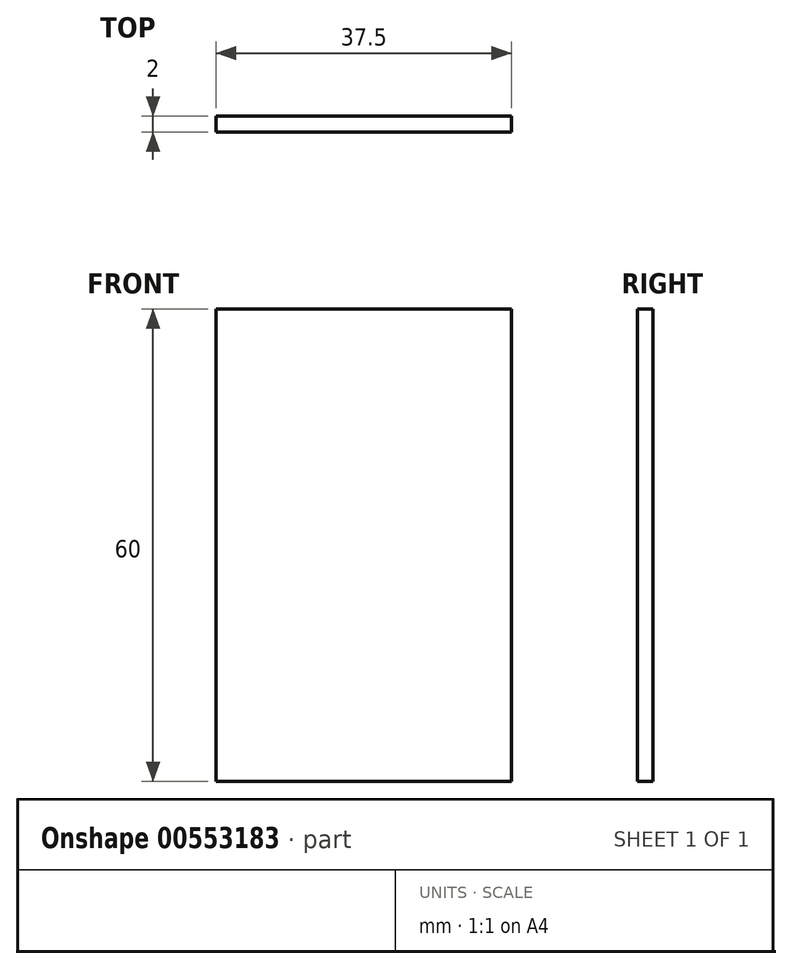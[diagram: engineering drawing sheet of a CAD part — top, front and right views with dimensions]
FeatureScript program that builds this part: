
annotation { "Feature Type Name" : "Feature", "Feature Type Description" : "" }
export const myFeature = defineFeature(function(context is Context, id is Id, definition is map)
    precondition{}
    {
        {
            var Q0;
            Q0=qCreatedBy(makeId("Front.planeOp"),FACE);
            var sketch = newSketch(context, id + "F0", { "sketchPlane" : qUnion([Q0])});
            skLineSegment(sketch, "E0.bottom", {"start": v(18.75, -30) * mm, "end": v(-18.75, -30) * mm});
            skLineSegment(sketch, "E0.top", {"start": v(18.75, 30) * mm, "end": v(-18.75, 30) * mm});
            skLineSegment(sketch, "E0.left", {"start": v(18.75, -30) * mm, "end": v(18.75, 30) * mm});
            skLineSegment(sketch, "E0.right", {"start": v(-18.75, -30) * mm, "end": v(-18.75, 30) * mm});
            skPoint(sketch, "E0.middle", {"position": v(0, 0) * mm});
            skSolve(sketch);
        }
        {
            var Q0;
            Q0 = qSketchRegion(id + "F0", true);
            extrude(context, id + "F1", {"entities" : qUnion([Q0]), "depth" : 2 * mm, "offsetDistance" : 25 * mm});
        }
    });
